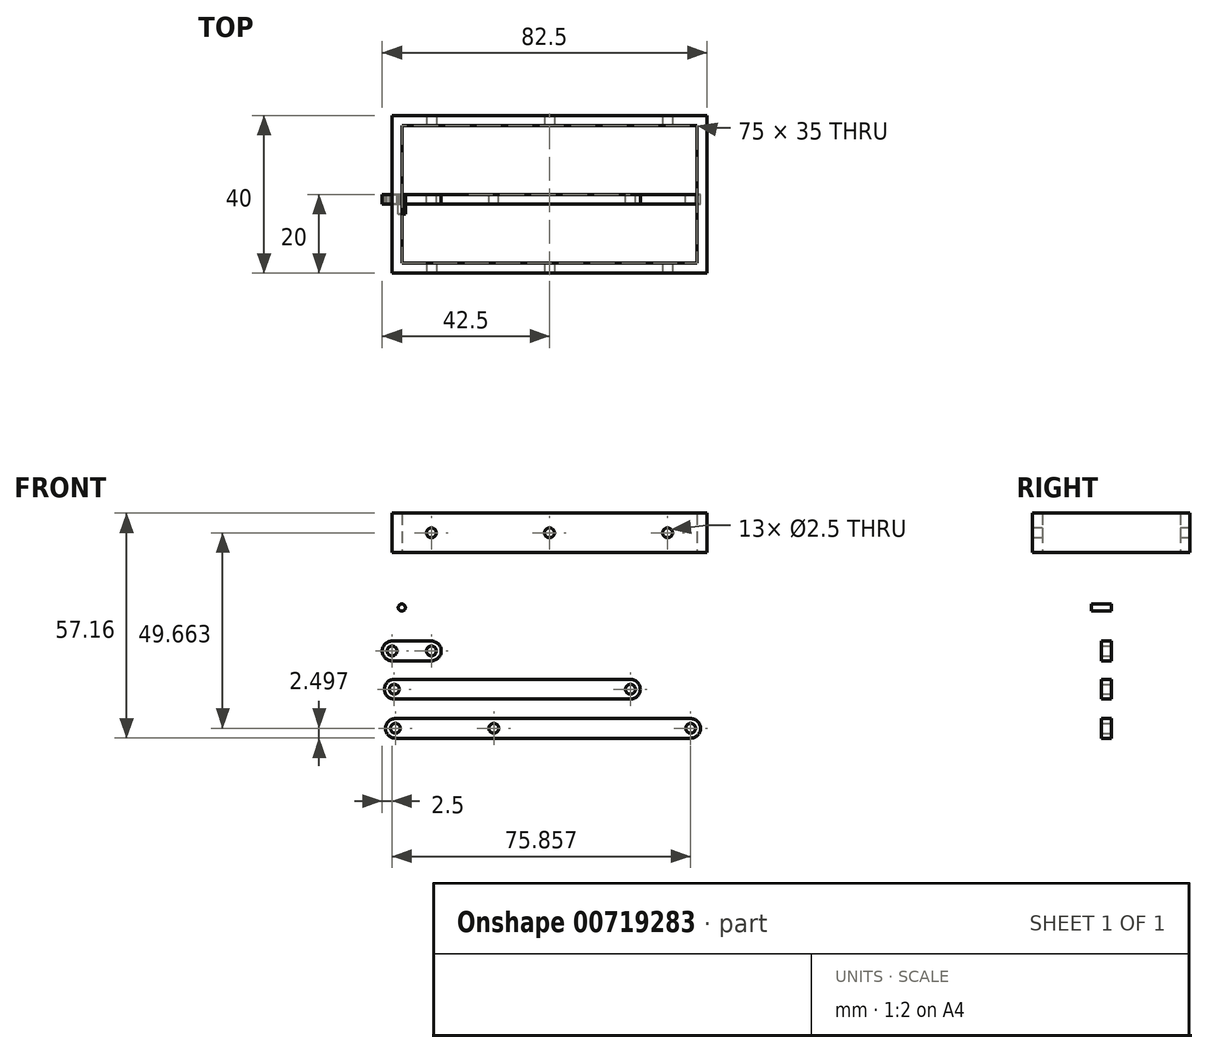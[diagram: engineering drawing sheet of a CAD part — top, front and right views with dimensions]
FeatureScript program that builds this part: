
annotation { "Feature Type Name" : "Feature", "Feature Type Description" : "" }
export const myFeature = defineFeature(function(context is Context, id is Id, definition is map)
    precondition{}
    {
        {
            assignVariable(context, id + "F0", {"name" : "thickness", "anyValue" : 2.5});
        }
        {
            var Q0;
            Q0=qCreatedBy(makeId("Front.planeOp"),FACE);
            var sketch = newSketch(context, id + "F1", { "sketchPlane" : qUnion([Q0])});
            skArc(sketch, "E0", {"start": v(0, 2.5) * mm, "mid": v(-2.5, 0) * mm, "end": v(0, -2.5) * mm});
            skArc(sketch, "E1", {"start": v(10, -2.5) * mm, "mid": v(12.5, 0) * mm, "end": v(10, 2.5) * mm});
            skLineSegment(sketch, "E2", {"start": v(0, 2.5) * mm, "end": v(10, 2.5) * mm});
            skLineSegment(sketch, "E3", {"start": v(0, -2.5) * mm, "end": v(10, -2.5) * mm});
            skCircle(sketch, "E4", {"center": v(0, 0) * mm, "radius": 1.25 * mm});
            skCircle(sketch, "E5", {"center": v(10, 0) * mm, "radius": 1.25 * mm});
            skSolve(sketch);
        }
        {
            var Q0;
            Q0=makeQuery(id+"F1.imprint","IMPRINT",FACE,{"disambiguationData":[TD([[makeQuery(id+"F1.imprint","IMPRINT",EDGE,{"derivedFrom":sQuery(id+"F1.wireOp",EDGE,"E0")}),1.0]])]});
            extrude(context, id + "F2", {"entities" : qUnion([Q0]), "depth" : (getVariable(context, 'thickness')) * mm, "offsetDistance" : 25 * mm});
        }
        {
            var Q0;
            Q0=qCreatedBy(makeId("Front.planeOp"),FACE);
            var sketch = newSketch(context, id + "F3", { "sketchPlane" : qUnion([Q0])});
            skArc(sketch, "E6", {"start": v(0.57, -7.23) * mm, "mid": v(-1.93, -9.73) * mm, "end": v(0.57, -12.23) * mm});
            skArc(sketch, "E7", {"start": v(60.57, -12.23) * mm, "mid": v(63.07, -9.73) * mm, "end": v(60.57, -7.23) * mm});
            skLineSegment(sketch, "E8", {"start": v(0.57, -7.23) * mm, "end": v(60.57, -7.23) * mm});
            skLineSegment(sketch, "E9", {"start": v(0.57, -12.23) * mm, "end": v(60.57, -12.23) * mm});
            skCircle(sketch, "E10", {"center": v(0.57, -9.73) * mm, "radius": 1.25 * mm});
            skCircle(sketch, "E11", {"center": v(60.57, -9.73) * mm, "radius": 1.25 * mm});
            skSolve(sketch);
        }
        {
            var Q0;
            Q0=makeQuery(id+"F3.imprint","IMPRINT",FACE,{"disambiguationData":[TD([[makeQuery(id+"F3.imprint","IMPRINT",EDGE,{"derivedFrom":sQuery(id+"F3.wireOp",EDGE,"E6")}),1.0]])]});
            extrude(context, id + "F4", {"entities" : qUnion([Q0]), "depth" : (getVariable(context, 'thickness')) * mm, "offsetDistance" : 25 * mm});
        }
        {
            var Q0;
            Q0=qCreatedBy(makeId("Front.planeOp"),FACE);
            var sketch = newSketch(context, id + "F5", { "sketchPlane" : qUnion([Q0])});
            skArc(sketch, "E12", {"start": v(0.86, -17.16) * mm, "mid": v(-1.64, -19.66) * mm, "end": v(0.86, -22.16) * mm});
            skArc(sketch, "E13", {"start": v(75.86, -22.16) * mm, "mid": v(78.36, -19.66) * mm, "end": v(75.86, -17.16) * mm});
            skLineSegment(sketch, "E14", {"start": v(0.86, -17.16) * mm, "end": v(75.86, -17.16) * mm});
            skLineSegment(sketch, "E15", {"start": v(0.86, -22.16) * mm, "end": v(75.86, -22.16) * mm});
            skCircle(sketch, "E16", {"center": v(0.86, -19.66) * mm, "radius": 1.25 * mm});
            skCircle(sketch, "E17", {"center": v(75.86, -19.66) * mm, "radius": 1.25 * mm});
            skCircle(sketch, "E18", {"center": v(25.86, -19.66) * mm, "radius": 1.25 * mm});
            skSolve(sketch);
        }
        {
            var Q0;
            Q0=makeQuery(id+"F5.imprint","IMPRINT",FACE,{"disambiguationData":[TD([[makeQuery(id+"F5.imprint","IMPRINT",EDGE,{"derivedFrom":sQuery(id+"F5.wireOp",EDGE,"E12")}),1.0]])]});
            extrude(context, id + "F6", {"entities" : qUnion([Q0]), "depth" : (getVariable(context, 'thickness')) * mm, "offsetDistance" : 25 * mm});
        }
        {
            var Q0;
            Q0=qCreatedBy(makeId("Top.planeOp"),FACE);
            cPlane(context, id + "F7", {"entities" : qUnion([Q0]), "cplaneType" : CPlaneType.OFFSET, "offset" : 25 * mm, "width" : 150 * mm, "height" : 150 * mm});
        }
        {
            var Q0;
            Q0=qCreatedBy(id+"F7.planeOp",FACE);
            var sketch = newSketch(context, id + "F8", { "sketchPlane" : qUnion([Q0])});
            skLineSegment(sketch, "E19.bottom", {"start": v(0, 20) * mm, "end": v(80, 20) * mm});
            skLineSegment(sketch, "E19.top", {"start": v(0, -20) * mm, "end": v(80, -20) * mm});
            skLineSegment(sketch, "E19.left", {"start": v(0, 20) * mm, "end": v(0, -20) * mm});
            skLineSegment(sketch, "E19.right", {"start": v(80, 20) * mm, "end": v(80, -20) * mm});
            skLineSegment(sketch, "E20.0", {"start": v(2.5, 17.5) * mm, "end": v(77.5, 17.5) * mm});
            skLineSegment(sketch, "E20.1", {"start": v(2.5, 17.5) * mm, "end": v(2.5, -17.5) * mm});
            skLineSegment(sketch, "E20.2", {"start": v(2.5, -17.5) * mm, "end": v(77.5, -17.5) * mm});
            skLineSegment(sketch, "E20.3", {"start": v(77.5, 17.5) * mm, "end": v(77.5, -17.5) * mm});
            skSolve(sketch);
        }
        {
            var Q0;
            Q0=makeQuery(id+"F8.imprint","IMPRINT",FACE,{"disambiguationData":[TD([[makeQuery(id+"F8.imprint","IMPRINT",EDGE,{"derivedFrom":sQuery(id+"F8.wireOp",EDGE,"E19.bottom")}),-1.0]])]});
            extrude(context, id + "F9", {"entities" : qUnion([Q0]), "depth" : 10 * mm, "offsetDistance" : 25 * mm});
        }
        {
            var Q0;
            Q0=makeQuery(id+"F9.opExtrude","SWEPT_FACE",FACE,{"disambiguationData":[OSD([sQuery(id+"F8.wireOp",EDGE,"E19.top")])]});
            var sketch = newSketch(context, id + "F10", { "sketchPlane" : qUnion([Q0])});
            skCircle(sketch, "E21", {"center": v(10, 30) * mm, "radius": 1.25 * mm});
            skCircle(sketch, "E22", {"center": v(70, 30) * mm, "radius": 1.25 * mm});
            skCircle(sketch, "E23", {"center": v(40, 30) * mm, "radius": 1.25 * mm});
            skPoint(sketch, "E23.centerSnap0", {"position": v(40, 25) * mm});
            skSolve(sketch);
        }
        {
            var Q0;
            Q0=qSketchRegion(id+"F10",true);
            extrude(context, id + "F11", {"entities" : qUnion([Q0]), "operationType" : NewBodyOperationType.REMOVE, "endBound" : BoundingType.THROUGH_ALL, "oppositeDirection" : true, "depth" : 25 * mm, "offsetDistance" : 25 * mm});
        }
        {
            var Q0;
            Q0=qCreatedBy(makeId("Front.planeOp"),FACE);
            var sketch = newSketch(context, id + "F12", { "sketchPlane" : qUnion([Q0])});
            skCircle(sketch, "E24", {"center": v(2.49, 11.02) * mm, "radius": 0.9 * mm});
            skSolve(sketch);
        }
        {
            var Q0;
            Q0=makeQuery(id+"F12.imprint","IMPRINT",FACE,{"disambiguationData":[TD([[makeQuery(id+"F12.imprint","IMPRINT",EDGE,{"derivedFrom":sQuery(id+"F12.wireOp",EDGE,"E24")}),1.0]])]});
            extrude(context, id + "F13", {"entities" : qUnion([Q0]), "depth" : (getVariable(context, 'thickness') * 2) * mm, "offsetDistance" : 25 * mm});
        }
    });
